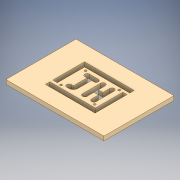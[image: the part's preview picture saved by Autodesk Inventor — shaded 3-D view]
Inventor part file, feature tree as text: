
AUTODESK INVENTOR PART (.ipt)
format: ipt  version: 2017 (Build 210142000, 142)  size: 305,152 bytes
history: native  units: mm
features: sketch x2, extrude x2
ambient origin geometry x8: Origin, YZ Plane, XZ Plane, XY Plane, X Axis, Y Axis, Z Axis, Center Point
bodies: Body1 (feature_tree)
feature tree (4):
  sketch  "Sketch1"  dims[d0=26.0mm d1=6.5mm d2=13.0mm d3=13.0mm d4=6.5mm d5=13.0mm d6=39.0mm d7=39.0mm d8=6.5mm d9=52.0mm d10=6.5mm d11=13.0mm d12=19.5mm d13=13.0mm d14=13.0mm d15=13.0mm d16=19.5mm d17=13.0mm d19=52.0mm d20=13.0mm d22=6.5mm d23=19.5mm d24=6.5mm d53=19.5mm d54=6.35mm]
  extrude  "Extrusion6"  Depth=19.5mm
  extrude  "Extrusion7"  Depth=12.0mm
  sketch  "Sketch2"  dims[d55=6.35mm d56=6.35mm d57=6.35mm d62=117.0mm d63=86.0mm d64=280.0mm d65=200.0mm d66=57.0mm d68=17.0mm d69=24.0mm d70=81.5mm d77=12.0mm d78=0.0mm d79=12.0mm d80=0.0mm]
